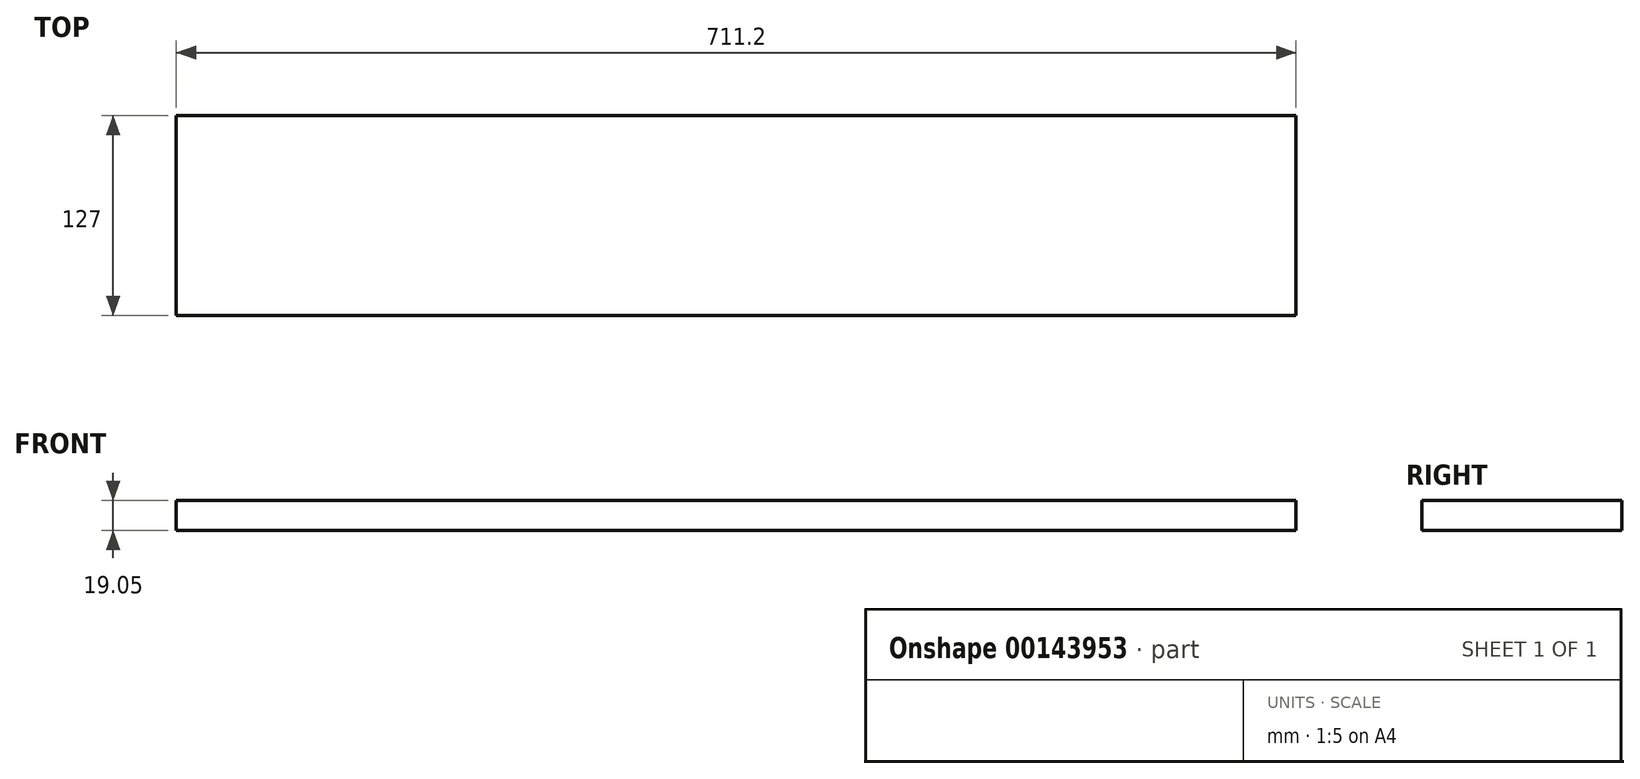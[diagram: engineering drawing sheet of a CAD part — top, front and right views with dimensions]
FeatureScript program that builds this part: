
annotation { "Feature Type Name" : "Feature", "Feature Type Description" : "" }
export const myFeature = defineFeature(function(context is Context, id is Id, definition is map)
    precondition{}
    {
        {
            var Q0;
            Q0=qCreatedBy(makeId("Top.planeOp"),FACE);
            var sketch = newSketch(context, id + "F0", { "sketchPlane" : qUnion([Q0])});
            skLineSegment(sketch, "E0.bottom", {"start": v(-214.91, 70.14) * mm, "end": v(496.29, 70.14) * mm});
            skLineSegment(sketch, "E0.top", {"start": v(-214.91, -56.86) * mm, "end": v(496.29, -56.86) * mm});
            skLineSegment(sketch, "E0.left", {"start": v(-214.91, 70.14) * mm, "end": v(-214.91, -56.86) * mm});
            skLineSegment(sketch, "E0.right", {"start": v(496.29, 70.14) * mm, "end": v(496.29, -56.86) * mm});
            skSolve(sketch);
        }
        {
            var Q0;
            Q0=makeQuery(id+"F0.imprint","IMPRINT",FACE,{"disambiguationData":[TD([[makeQuery(id+"F0.imprint","IMPRINT",EDGE,{"derivedFrom":sQuery(id+"F0.wireOp",EDGE,"E0.bottom")}),-1.0]])]});
            extrude(context, id + "F1", {"entities" : qUnion([Q0]), "depth" : 19.05 * mm});
        }
    });
